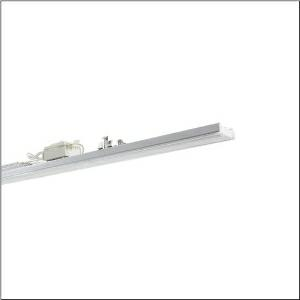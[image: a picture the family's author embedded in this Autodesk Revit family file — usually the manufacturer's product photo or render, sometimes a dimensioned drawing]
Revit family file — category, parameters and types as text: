
# Revit family: licross_r__11_recessed_mo_51tl10de445g_6e9c
name_source: partatom
category: Lighting Fixtures
units: mm (PartAtom-declared; Revit-internal decimal feet)

## family parameters
Cut with Voids When Loaded = No
Host = Face
Light Source = No
Part Type = Normal
Room Calculation Point = No
Round Connector Dimension = Use Diameter
Shared = No

## types (1)
- --- (1 x LED, 4980 lm, 29.6 W, 4000K)
    Apparent Load = 30 VA
    CIE Flux Codes = 50 81 96 100 100
    Color Rendering = 80
    Color Temperature = 4000K
    Default Elevation = 1800 mm
    Description = Licross® 11 Recessed MO, luminaire insert, of sheet steel, coil coated, white, length: 750mm, width: 66mm, height: 67mm, LED rated luminous flux: 4.980lm, light colour: 840, control gear: DALI 2, with plug, 5-pole, with phase selection, mains connection: 220..240V, AC, 50/60Hz, rated input power: 30W, internal wiring halogen-free, primary optical cover: cover, of PMMA, light emission: direct distribution, primary light characteristic: symmetric, protection rating (complete): IP40, insulation class (complete): insulation class I (protective earthing), certification: CE, ENEC, VDE, UKCA, protection symbol: D if used in an environment without relevant dust loads with corresponding accessories, impact resistance: IK06, permissible ambient temperature for indoor applications: -25..+35°C, corresponds to IFS (International Featured Standards) requirements for safety and quality in the food industry, reducing of maximum allowable ambient temperature of 5°C with ceiling mounting, LABS conformity tested according to VDMA 24364:2018-05, packaging unit: 1 piece
    Height = 58 mm
    Lamp = 1 x LED
    Lamp Light Flux = 4980 lm
    Lamp Power = 29.6 W
    Lamp count = 1
    Length = 750 mm
    Luminous efficacy = 168 lm/W
    Manufacturer = Siteco
    ModVariant = No
    Model = 51TL10DE445G
    Mounting Place = Ceiling
    Mounting Type = Pendant
    Number of Poles = 1
    OnlyDefault = Yes
    Power Factor = 1
    Product Name = Licross® 11 Recessed MO
    Product group = luminaire insert | ceiling pendant
    ProductGroupID = 902
    Protection Class = Protection class I
    Protection Degree = IP 40
    RLX_Detail_Level = 1
    RLX_Emergency_Light_Flux = 0 lm
    RLX_Emergency_Type = 0
    RLX_Emergency_Type_DB = No
    RlxData = <blob elided: 29197 chars, md5=d16ee3e1>
    Socket = socket
    Standby Power = 0 W
    System Light Flux = 4980 lm
    System Power = 30 W
    Type Comments = factory setting: luminous flux: 100 % | dim-lin: 254 | 378 mA
    Type Image = l_1296930.jpg
    URL = http://relux.com
    VarID = @adj_121123
    Voltage = 0 V
    Weight = 0.00 kg
    Width = 66 mm

## geometry (parser evidence)
native form markers: Blend x4, Sweep x9
no freeform markers — native parametric forms only
